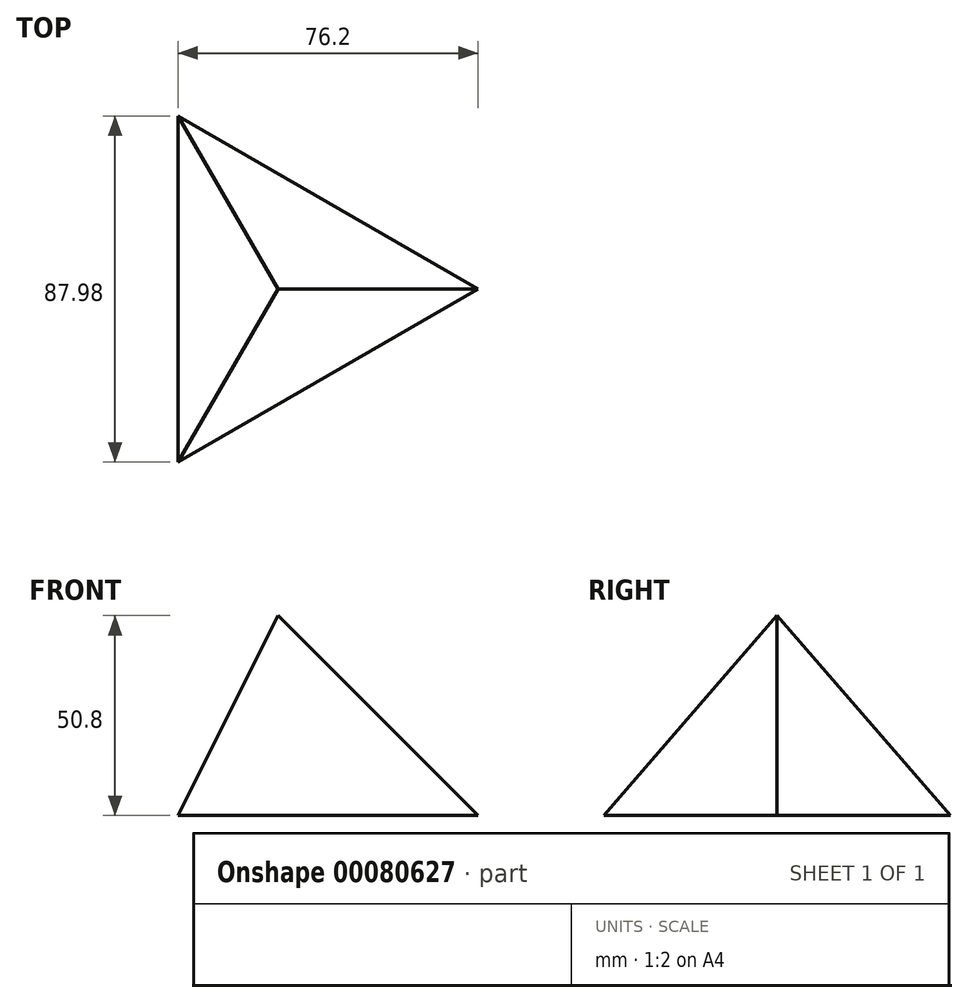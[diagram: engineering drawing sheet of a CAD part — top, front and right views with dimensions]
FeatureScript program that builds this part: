
annotation { "Feature Type Name" : "Feature", "Feature Type Description" : "" }
export const myFeature = defineFeature(function(context is Context, id is Id, definition is map)
    precondition{}
    {
        {
            var Q0;
            Q0=qCreatedBy(makeId("Top.planeOp"),FACE);
            var sketch = newSketch(context, id + "F0", { "sketchPlane" : qUnion([Q0])});
            skCircle(sketch, "E0.cCircle", {"center": v(0, 0) * mm, "radius": 25.4 * mm, "construction": true});
            skLineSegment(sketch, "E0.0", {"start": v(-25.4, -44) * mm, "end": v(-25.4, 44) * mm});
            skLineSegment(sketch, "E0.1", {"start": v(-25.4, 44) * mm, "end": v(50.8, 0) * mm});
            skLineSegment(sketch, "E0.2", {"start": v(50.8, 0) * mm, "end": v(-25.4, -44) * mm});
            skPoint(sketch, "E0.0.midPoint", {"position": v(-25.4, 0) * mm});
            skSolve(sketch);
        }
        {
            var Q0;
            Q0=qCreatedBy(makeId("Front.planeOp"),FACE);
            var sketch = newSketch(context, id + "F1", { "sketchPlane" : qUnion([Q0])});
            skLineSegment(sketch, "E1", {"start": v(0, 0) * mm, "end": v(0, 50.8) * mm});
            skSolve(sketch);
        }
        {
            var Q0;
            Q0=makeQuery(id+"F0.imprint","IMPRINT",FACE,{"disambiguationData":[TD([[makeQuery(id+"F0.imprint","IMPRINT",EDGE,{"derivedFrom":sQuery(id+"F0.wireOp",EDGE,"E0.0")}),-1.0]])]});
            var Q1;
            Q1=sQuery(id+"F1.wireOp",VERTEX,"E1.end");
            loft(context, id + "F2", {"sheetProfilesArray" : [{ "sheetProfileEntities" : qUnion([Q0]) }, { "sheetProfileEntities" : qUnion([Q1]) }]});
        }
    });
